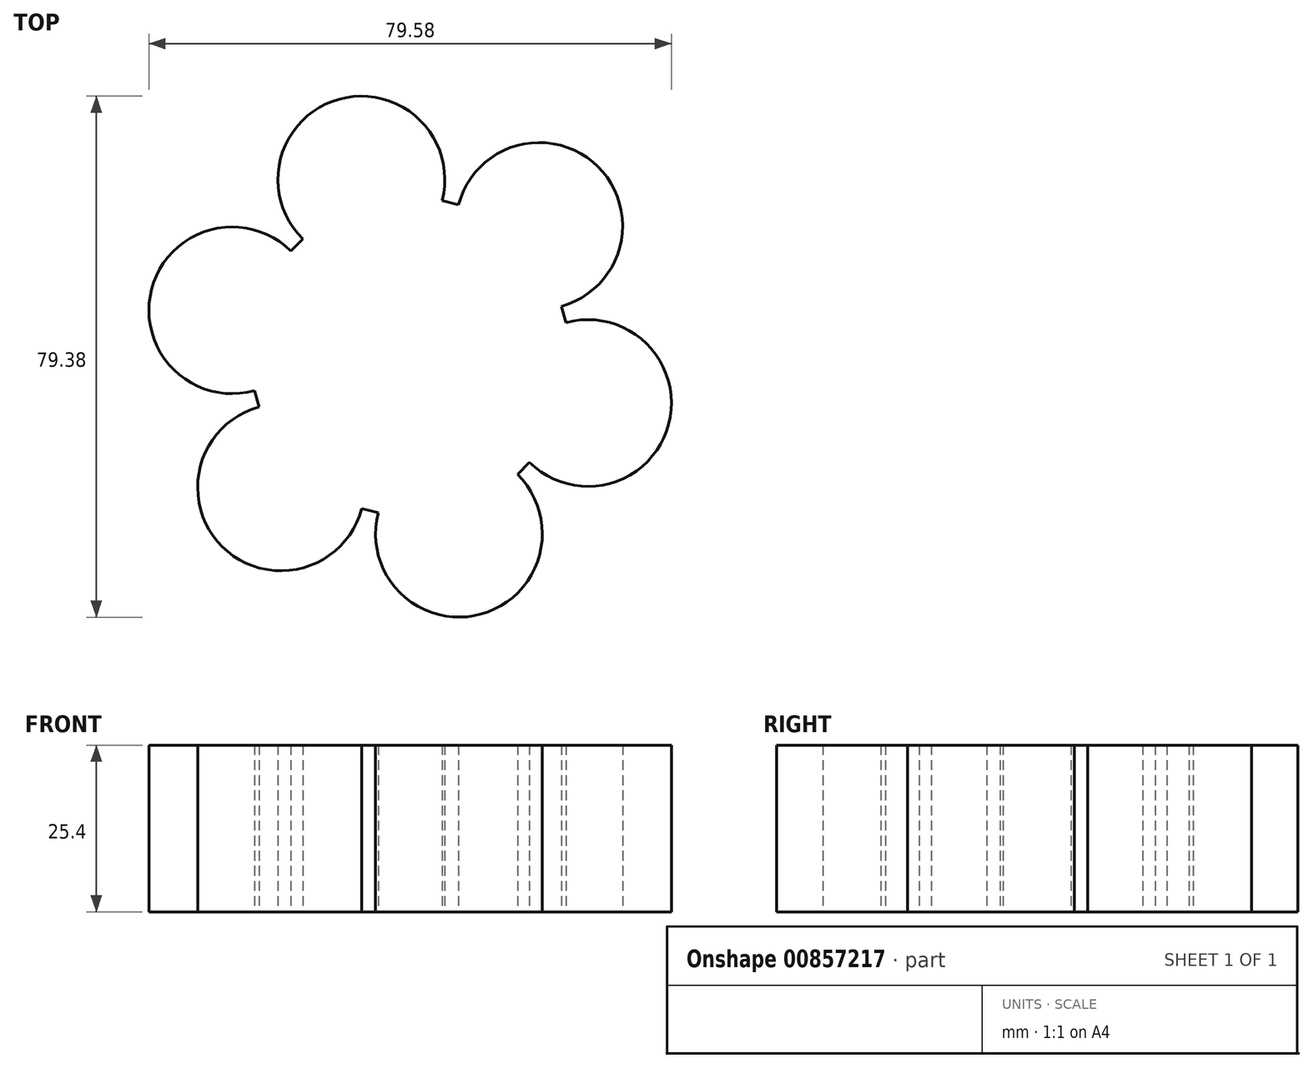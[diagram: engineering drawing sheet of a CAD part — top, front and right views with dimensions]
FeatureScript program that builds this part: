
annotation { "Feature Type Name" : "Feature", "Feature Type Description" : "" }
export const myFeature = defineFeature(function(context is Context, id is Id, definition is map)
    precondition{}
    {
        {
            var Q0;
            Q0=qCreatedBy(makeId("Top.planeOp"),FACE);
            var sketch = newSketch(context, id + "F0", { "sketchPlane" : qUnion([Q0])});
            skCircle(sketch, "E0", {"center": v(0, 0) * mm, "radius": 12.7 * mm});
            skCircle(sketch, "E1.cCircle", {"center": v(0, 0) * mm, "radius": 28 * mm, "construction": true});
            skLineSegment(sketch, "E1.0", {"start": v(-7.43, 26.99) * mm, "end": v(19.66, 19.93) * mm});
            skLineSegment(sketch, "E1.1", {"start": v(19.66, 19.93) * mm, "end": v(27.09, -7.06) * mm});
            skLineSegment(sketch, "E1.2", {"start": v(27.09, -7.06) * mm, "end": v(7.43, -26.99) * mm});
            skLineSegment(sketch, "E1.3", {"start": v(7.43, -26.99) * mm, "end": v(-19.66, -19.93) * mm});
            skLineSegment(sketch, "E1.4", {"start": v(-19.66, -19.93) * mm, "end": v(-27.09, 7.06) * mm});
            skLineSegment(sketch, "E1.5", {"start": v(-27.09, 7.06) * mm, "end": v(-7.43, 26.99) * mm});
            skCircle(sketch, "E2", {"center": v(19.66, 19.93) * mm, "radius": 12.7 * mm});
            skCircle(sketch, "E3", {"center": v(-7.43, 26.99) * mm, "radius": 12.7 * mm});
            skCircle(sketch, "E4", {"center": v(-27.09, 7.06) * mm, "radius": 12.7 * mm});
            skCircle(sketch, "E5", {"center": v(-19.66, -19.93) * mm, "radius": 12.7 * mm});
            skCircle(sketch, "E6", {"center": v(7.43, -26.99) * mm, "radius": 12.7 * mm});
            skCircle(sketch, "E7", {"center": v(27.09, -7.06) * mm, "radius": 12.7 * mm});
            skSolve(sketch);
        }
        {
            var Q0;
            {var subQ0=sQuery(id+"F0.wireOp",EDGE,"E1.5");var subQ1=sQuery(id+"F0.wireOp",EDGE,"E1.0");var subQ2=makeQuery(id+"F0.imprint","INTERSECT",VERTEX,{"derivedFrom":[subQ1,subQ0]});Q0=makeQuery(id+"F0.imprint","IMPRINT",FACE,{"disambiguationData":[TD([[makeQuery(id+"F0.imprint","IMPRINT",EDGE,{"disambiguationData":[TD([[subQ2,-1.0]])],"derivedFrom":subQ1}),-1.0]])]});}
            var Q1;
            {var subQ0=sQuery(id+"F0.wireOp",EDGE,"E1.2");var subQ1=sQuery(id+"F0.wireOp",EDGE,"E1.1");var subQ2=makeQuery(id+"F0.imprint","INTERSECT",VERTEX,{"derivedFrom":[subQ1,subQ0]});Q1=makeQuery(id+"F0.imprint","IMPRINT",FACE,{"disambiguationData":[TD([[makeQuery(id+"F0.imprint","IMPRINT",EDGE,{"disambiguationData":[TD([[subQ2,1.0]])],"derivedFrom":subQ1}),-1.0]])]});}
            var Q2;
            {var subQ0=sQuery(id+"F0.wireOp",EDGE,"E1.2");var subQ1=sQuery(id+"F0.wireOp",EDGE,"E1.1");var subQ2=makeQuery(id+"F0.imprint","INTERSECT",VERTEX,{"derivedFrom":[subQ1,subQ0]});Q2=makeQuery(id+"F0.imprint","IMPRINT",FACE,{"disambiguationData":[TD([[makeQuery(id+"F0.imprint","IMPRINT",EDGE,{"disambiguationData":[TD([[subQ2,1.0]])],"derivedFrom":subQ1}),1.0]])]});}
            var Q3;
            Q3=makeQuery(id+"F0.imprint","IMPRINT",FACE,{"disambiguationData":[TD([[makeQuery(id+"F0.imprint","IMPRINT",EDGE,{"derivedFrom":sQuery(id+"F0.wireOp",EDGE,"E0")}),1.0]])]});
            var Q4;
            {var subQ0=sQuery(id+"F0.wireOp",EDGE,"E1.1");var subQ1=sQuery(id+"F0.wireOp",EDGE,"E1.0");var subQ2=makeQuery(id+"F0.imprint","INTERSECT",VERTEX,{"derivedFrom":[subQ1,subQ0]});Q4=makeQuery(id+"F0.imprint","IMPRINT",FACE,{"disambiguationData":[TD([[makeQuery(id+"F0.imprint","IMPRINT",EDGE,{"disambiguationData":[TD([[subQ2,1.0]])],"derivedFrom":subQ1}),-1.0]])]});}
            var Q5;
            {var subQ0=sQuery(id+"F0.wireOp",EDGE,"E1.3");var subQ1=sQuery(id+"F0.wireOp",EDGE,"E1.2");var subQ2=makeQuery(id+"F0.imprint","INTERSECT",VERTEX,{"derivedFrom":[subQ1,subQ0]});Q5=makeQuery(id+"F0.imprint","IMPRINT",FACE,{"disambiguationData":[TD([[makeQuery(id+"F0.imprint","IMPRINT",EDGE,{"disambiguationData":[TD([[subQ2,1.0]])],"derivedFrom":subQ1}),1.0]])]});}
            var Q6;
            {var subQ0=sQuery(id+"F0.wireOp",EDGE,"E1.5");var subQ1=sQuery(id+"F0.wireOp",EDGE,"E1.4");var subQ2=makeQuery(id+"F0.imprint","INTERSECT",VERTEX,{"derivedFrom":[subQ1,subQ0]});Q6=makeQuery(id+"F0.imprint","IMPRINT",FACE,{"disambiguationData":[TD([[makeQuery(id+"F0.imprint","IMPRINT",EDGE,{"disambiguationData":[TD([[subQ2,1.0]])],"derivedFrom":subQ1}),1.0]])]});}
            var Q7;
            {var subQ0=sQuery(id+"F0.wireOp",EDGE,"E1.1");var subQ1=sQuery(id+"F0.wireOp",EDGE,"E1.0");var subQ2=makeQuery(id+"F0.imprint","INTERSECT",VERTEX,{"derivedFrom":[subQ1,subQ0]});Q7=makeQuery(id+"F0.imprint","IMPRINT",FACE,{"disambiguationData":[TD([[makeQuery(id+"F0.imprint","IMPRINT",EDGE,{"disambiguationData":[TD([[subQ2,1.0]])],"derivedFrom":subQ1}),1.0]])]});}
            var Q8;
            {var subQ0=sQuery(id+"F0.wireOp",EDGE,"E1.5");var subQ1=sQuery(id+"F0.wireOp",EDGE,"E1.4");var subQ2=makeQuery(id+"F0.imprint","INTERSECT",VERTEX,{"derivedFrom":[subQ1,subQ0]});Q8=makeQuery(id+"F0.imprint","IMPRINT",FACE,{"disambiguationData":[TD([[makeQuery(id+"F0.imprint","IMPRINT",EDGE,{"disambiguationData":[TD([[subQ2,1.0]])],"derivedFrom":subQ1}),-1.0]])]});}
            var Q9;
            Q9=makeQuery(id+"F0.imprint","IMPRINT",FACE,{"disambiguationData":[TD([[makeQuery(id+"F0.imprint","IMPRINT",EDGE,{"derivedFrom":sQuery(id+"F0.wireOp",EDGE,"E0")}),-1.0]])]});
            var Q10;
            {var subQ0=sQuery(id+"F0.wireOp",EDGE,"E1.4");var subQ1=sQuery(id+"F0.wireOp",EDGE,"E1.3");var subQ2=makeQuery(id+"F0.imprint","INTERSECT",VERTEX,{"derivedFrom":[subQ1,subQ0]});Q10=makeQuery(id+"F0.imprint","IMPRINT",FACE,{"disambiguationData":[TD([[makeQuery(id+"F0.imprint","IMPRINT",EDGE,{"disambiguationData":[TD([[subQ2,1.0]])],"derivedFrom":subQ1}),-1.0]])]});}
            var Q11;
            {var subQ0=sQuery(id+"F0.wireOp",EDGE,"E1.5");var subQ1=sQuery(id+"F0.wireOp",EDGE,"E1.0");var subQ2=makeQuery(id+"F0.imprint","INTERSECT",VERTEX,{"derivedFrom":[subQ1,subQ0]});Q11=makeQuery(id+"F0.imprint","IMPRINT",FACE,{"disambiguationData":[TD([[makeQuery(id+"F0.imprint","IMPRINT",EDGE,{"disambiguationData":[TD([[subQ2,-1.0]])],"derivedFrom":subQ1}),1.0]])]});}
            var Q12;
            {var subQ0=sQuery(id+"F0.wireOp",EDGE,"E1.3");var subQ1=sQuery(id+"F0.wireOp",EDGE,"E1.2");var subQ2=makeQuery(id+"F0.imprint","INTERSECT",VERTEX,{"derivedFrom":[subQ1,subQ0]});Q12=makeQuery(id+"F0.imprint","IMPRINT",FACE,{"disambiguationData":[TD([[makeQuery(id+"F0.imprint","IMPRINT",EDGE,{"disambiguationData":[TD([[subQ2,1.0]])],"derivedFrom":subQ1}),-1.0]])]});}
            var Q13;
            {var subQ0=sQuery(id+"F0.wireOp",EDGE,"E1.4");var subQ1=sQuery(id+"F0.wireOp",EDGE,"E1.3");var subQ2=makeQuery(id+"F0.imprint","INTERSECT",VERTEX,{"derivedFrom":[subQ1,subQ0]});Q13=makeQuery(id+"F0.imprint","IMPRINT",FACE,{"disambiguationData":[TD([[makeQuery(id+"F0.imprint","IMPRINT",EDGE,{"disambiguationData":[TD([[subQ2,1.0]])],"derivedFrom":subQ1}),1.0]])]});}
            extrude(context, id + "F1", {"entities" : qUnion([Q0, Q1, Q2, Q3, Q4, Q5, Q6, Q7, Q8, Q9, Q10, Q11, Q12, Q13]), "depth" : 25.4 * mm, "offsetDistance" : 25.4 * mm});
        }
    });
